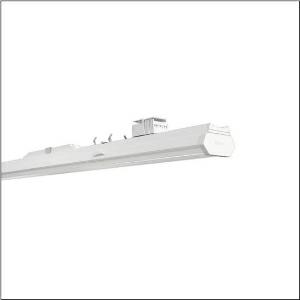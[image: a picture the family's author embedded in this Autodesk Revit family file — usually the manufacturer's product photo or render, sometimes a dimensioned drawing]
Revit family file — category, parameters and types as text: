
# Revit family: licross_21_protected_ho_52td12dn4e5m
name_source: partatom
category: Lighting Fixtures
units: mm (PartAtom-declared; Revit-internal decimal feet)

## family parameters
Cut with Voids When Loaded = No
Host = Face
Light Source = No
Part Type = Normal
Room Calculation Point = No
Round Connector Dimension = Use Diameter
Shared = No

## types (1)
- --- (1 x LED, 14690 lm, 84.9 W, 4000K)
    Apparent Load = 85 VA
    CIE Flux Codes = 70 91 97 98 100
    Color Rendering = 80
    Color Temperature = 4000K
    Default Elevation = 1800 mm
    Description = Licross 21 Protected HO, luminaire insert, of sheet steel, galvanised, coil coated, white, length: 1.500mm, width: 90mm, height: 103mm, LED rated luminous flux: 14.690lm, light colour: 840, SDCM (Standard Deviation of Colour Matching)MacAdam ≤ 3 SDCM (initial), control gear: DALI 2, with plug, 5-pole, with phase selection, mains connection: 220..240V, AC, 50/60Hz, rated input power: 85W, internal wiring halogen-free, primary light control with lens, of plastic, primary optical cover: cover, of PMMA, light emission: direct distribution, primary light characteristic: symmetric, protection rating (complete): IP54, insulation class (complete): insulation class I (protective earthing), certification: CE, ENEC, VDE, UKCA, protection symbol: D if used in an environment with non-conductive dust loads with corresponding accessories, impact resistance: IK06, permissible ambient temperature for indoor applications: -25..+35°C, corresponds to IFS (International Featured Standards) requirements for safety and quality in the food industry, reducing of maximum allowable ambient temperature of 5°C with ceiling mounting, LABS conformity tested according to VDMA 24364:2018-05, The light source and the operating device comply with the requirements of the Ecodesign Regulation (EU) 2019/2020 and are replaceable in accordance with this regulation, packaging unit: 1 piece
    Height = 92 mm
    Lamp = 1 x LED
    Lamp Light Flux = 14690 lm
    Lamp Power = 84.9 W
    Lamp count = 1
    Length = 1500 mm
    Luminous efficacy = 173 lm/W
    Manufacturer = Siteco
    ModVariant = No
    Model = 52TD12DN4E5M
    Mounting Place = Ceiling
    Mounting Type = Pendant
    Number of Poles = 1
    OnlyDefault = Yes
    Power Factor = 1
    Product Name = Licross 21 Protected HO
    Product group = luminaire insert | ceiling pendant
    ProductGroupID = 901
    Protection Class = Protection class I
    Protection Degree = IP 54
    RLX_Detail_Level = 1
    RLX_Emergency_Light_Flux = 0 lm
    RLX_Emergency_Type = 0
    RLX_Emergency_Type_DB = No
    RlxData = <blob elided: 24821 chars, md5=6c956c40>
    Socket = socket
    Standby Power = 0 W
    System Light Flux = 14690 lm
    System Power = 85 W
    Type Comments = factory setting: luminous flux: 100 % | dim-lin: 254 | 484 mA
    Type Image = l_1256148.jpg
    URL = http://relux.com
    VarID = @adj_129177
    Voltage = 0 V
    Weight = 0.00 kg
    Width = 88 mm

## geometry (parser evidence)
native form markers: Blend x4, Sweep x11
no freeform markers — native parametric forms only
